# Revit family: IS_Extra_BD521_BIM_GB
name_source: partatom
category: Plumbing Fixtures
units: mm (PartAtom-declared; Revit-internal decimal feet)

## family parameters
Always vertical = No
Cut with Voids When Loaded = No
OmniClass Number = 23.45.55.14
OmniClass Title = Single Faucets
Part Type = Normal
Room Calculation Point = No
Round Connector Dimension = Use Diameter
Shared = No
Work Plane-Based = No

## types (4) — shared parameters
Accessories = https://www.idealstandard.co.uk
AreaUnits = millimetres
BIMObjectName = Pillartaps_Extra_BD521_IdealStandard
BIMobject category = Taps & Mixers
BIMobject category code = sanitary-taps-mixers
BIMobject main category = Sanitary
BIMobject main category code = sanitary
Brand = Ideal standard
Brand url = http://www.idealstandard.co.uk
Category = Sanitary
Classification = Taps & Mixers
ConnectionType = plumbing
CurrencyUnit = £
CurrentRevision = 1
Date of publishing = 09/11/2022
Description = Pillar Tap (cold water)
DurationUnit = years
Edition number = 1
ElementType = Fixed
ExpectedLife = 5
FaucetFunction = Single lever shower and bath Mixer
FaucetOperation = Single lever shower and bath Mixer
FaucetTopDescription = Single lever shower and bath Mixer
FaucetType = Single lever shower and bath Mixer
Features = Pillar Tap (cold water)
Help = https://www.idealstandard.co.uk
IFC Classification = Sanitary Terminal
IfcExportAs = IfcValveType
IfcExportType = FAUCET
Installation instructions = https://www.idealstandard.co.uk
InstallationInstructions = https://www.idealstandard.co.uk
LinearUnits = millimetres
MaintenanceInformation = https://www.idealstandard.co.uk
Manufacturer = Ideal Standard
Manufacturer name = Ideal Standard
ManufacturerURL = https://www.idealstandard.co.uk
Masterformat 2014 Code = 22 40 00
Masterformat 2014 Description = Plumbing Fixtures
Material = Brass
Material main = Brass
NBS Reference Code = 45-35-70/371
NBS Reference Description = Taps and water supply fittings for wash basins and troughs
Name = IS_IdealStandard_Pillartaps_Extra_BD521
NettWeight = 1.037
NominalHeight = 130 mm
NominalWidth = 55 mm  [stored 0.180446 ft]
OmniClass Code = 23-31 11 00
OmniClass Description = Faucets
PredefinedType = Fixed
Product Guid = 2b420875-e846-48e4-a407-fd851d388437
Product SKU = BD521
Product certification = https://www.idealstandard.co.uk
Product data url = https://bimobject.com
Product family = Extra
Product group = Taps & Mixers
Product name = Pillar Tap (cold water)
Product url = https://www.idealstandard.co.uk
ProductInformation = https://www.idealstandard.co.uk
QR code = http://bimobject.com
Shape = cylindrical
Size = 150 x 130 x 55 mm
Space = Internal
SpareParts = https://www.idealstandard.co.uk
Technical description = https://www.idealstandard.co.uk
UNSPSC Code = 301815
URL = https://www.idealstandard.co.uk
Uniclass 1.4 Code = Mixer taps
Uniclass 1.4 Description = L725111
Uniclass 2.0 Code = Ac_20_64_30
Uniclass 2.0 Description = Fitting
Uniclass 2015 Code = Pr_40_20_87_96
Uniclass 2015 Name = Washbasin manual water supply sets
Uniclass2015Code = Pr_40_20_87_60
Uniclass2015Title = Pillar taps
Uniclass2015Version = v1.27
Uniformat II Code = Plumbing Fixtures
Uniformat II Description = D2010
ValveMechanism = Single lever shower and bath Mixer
ValveOperation = Single lever shower and bath Mixer
Version = 1
VolumeUnits = Liters
WRASURL = https://www.wrasapprovals.co.uk
WarrantyDescription = manufacturer warranty
WarrantyDurationUnit = years
Weight Net (Kg) = 1.037
Youtube clip = https://www.youtube.com
zero-valued in all types: NominalDepth, NominalLength

## per-type parameters (varying)
| type | BarCode | Color | Finish | GTIN code | MainColor | Model | ModelNumber | ModelReference |
| BD521AA - Pillar Tap (cold water) - Chrome | 3800861111474 | Chrome | Chrome | https://3800861111474 | Chrome | BD521AA | BD521AA | Pillar Tap (cold water) - Chrome |
| BD521A2 - Pillar Tap (cold water) - Brushed Gold | 3800861111863 | Brush Gold | Brush Gold | https://3800861111863 | Brush Gold | BD521A2 | BD521A2 | Pillar Tap (cold water) - Brushed Gold |
| BD521A5 - Pillar Tap (cold water) - Magnetic Grey | 3800861112259 | Magnetic Grey | Magnetic Grey | https://3800861112259 | Magnetic Grey | BD521A5 | BD521A5 | Pillar Tap (cold water) - Magnetic Grey |
| BD521GN - Pillar Tap (cold water) - Stainless Steel | 3800861112648 | Silver Storm | Silver Storm | https://3800861112648 | Silver Storm | BD521GN | BD521GN | Pillar Tap (cold water) - Stainless Steel |

note: [stored X ft] marks values corroborated as IEEE doubles in the binary element streams (Revit-internal decimal feet)

## geometry (parser evidence)
native form markers: Sweep x4
no freeform markers — native parametric forms only
